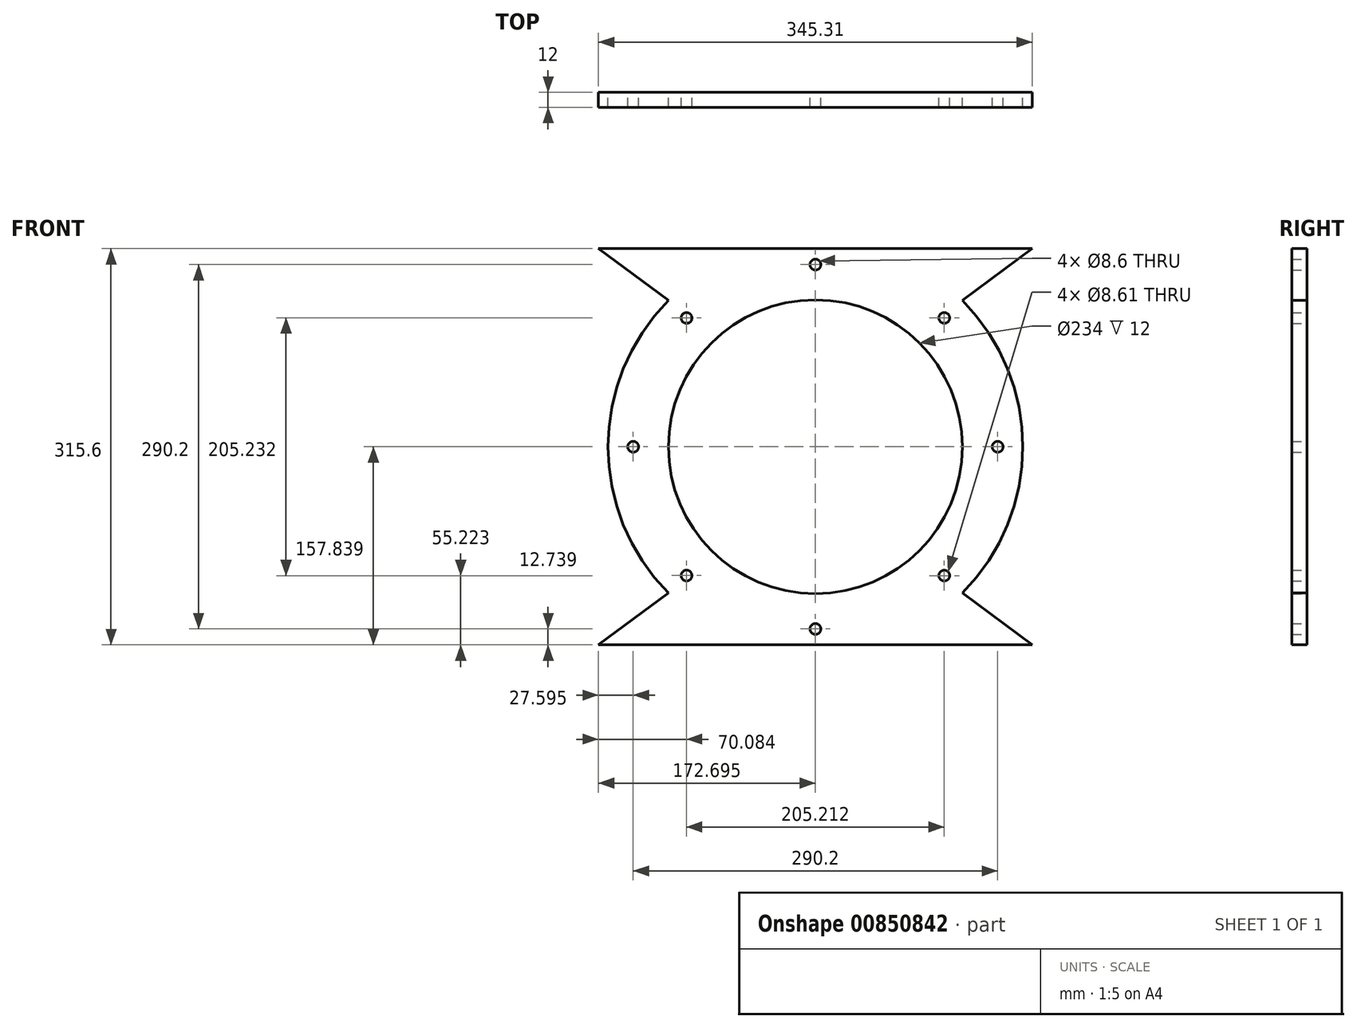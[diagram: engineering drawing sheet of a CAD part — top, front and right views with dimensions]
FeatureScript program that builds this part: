
annotation { "Feature Type Name" : "Feature", "Feature Type Description" : "" }
export const myFeature = defineFeature(function(context is Context, id is Id, definition is map)
    precondition{}
    {
        {
            var Q0;
            Q0=qCreatedBy(makeId("Front.planeOp"),FACE);
            var sketch = newSketch(context, id + "F0", { "sketchPlane" : qUnion([Q0])});
            skLineSegment(sketch, "E0", {"start": v(-224.43, -28.32) * mm, "end": v(120.88, -28.32) * mm});
            skLineSegment(sketch, "E1", {"start": v(-224.43, 287.28) * mm, "end": v(120.88, 287.28) * mm});
            skLineSegment(sketch, "E2", {"start": v(-224.43, 287.28) * mm, "end": v(-168.64, 246.1) * mm});
            skLineSegment(sketch, "E3", {"start": v(65.17, 246.1) * mm, "end": v(120.88, 287.28) * mm});
            skLineSegment(sketch, "E4", {"start": v(-168.64, 12.94) * mm, "end": v(-224.43, -28.32) * mm});
            skLineSegment(sketch, "E5", {"start": v(65.17, 12.94) * mm, "end": v(120.88, -28.32) * mm});
            skPoint(sketch, "E6.centerSnap0", {"position": v(-51.78, 287.28) * mm});
            skCircle(sketch, "E7", {"center": v(-51.73, 129.52) * mm, "radius": 117 * mm});
            skArc(sketch, "E8", {"start": v(-168.64, 246.1) * mm, "mid": v(-216.83, 129.52) * mm, "end": v(-168.64, 12.94) * mm});
            skArc(sketch, "E9", {"start": v(65.17, 246.1) * mm, "mid": v(113.37, 129.52) * mm, "end": v(65.17, 12.94) * mm});
            skCircle(sketch, "E10", {"center": v(-51.73, 274.62) * mm, "radius": 4.3 * mm});
            skCircle(sketch, "E11", {"center": v(-51.73, -15.58) * mm, "radius": 4.3 * mm});
            skCircle(sketch, "E12", {"center": v(93.37, 129.52) * mm, "radius": 4.3 * mm});
            skCircle(sketch, "E13", {"center": v(-196.83, 129.52) * mm, "radius": 4.3 * mm});
            skCircle(sketch, "E14", {"center": v(-154.35, 232.12) * mm, "radius": 4.3 * mm});
            skCircle(sketch, "E15", {"center": v(-154.34, 26.93) * mm, "radius": 4.3 * mm});
            skCircle(sketch, "E16", {"center": v(50.87, 26.9) * mm, "radius": 4.3 * mm});
            skCircle(sketch, "E17", {"center": v(50.87, 232.14) * mm, "radius": 4.3 * mm});
            skSolve(sketch);
        }
        {
            var Q0;
            {var subQ3=sQuery(id+"F0.wireOp",EDGE,"E0");Q0=makeQuery(id+"F0.imprint","IMPRINT",FACE,{"disambiguationData":[TD([[makeQuery(id+"F0.imprint","IMPRINT",EDGE,{"derivedFrom":subQ3}),1.0]])]});}
            extrude(context, id + "F1", {"entities" : qUnion([Q0]), "depth" : 12 * mm, "offsetDistance" : 25.4 * mm});
        }
    });
